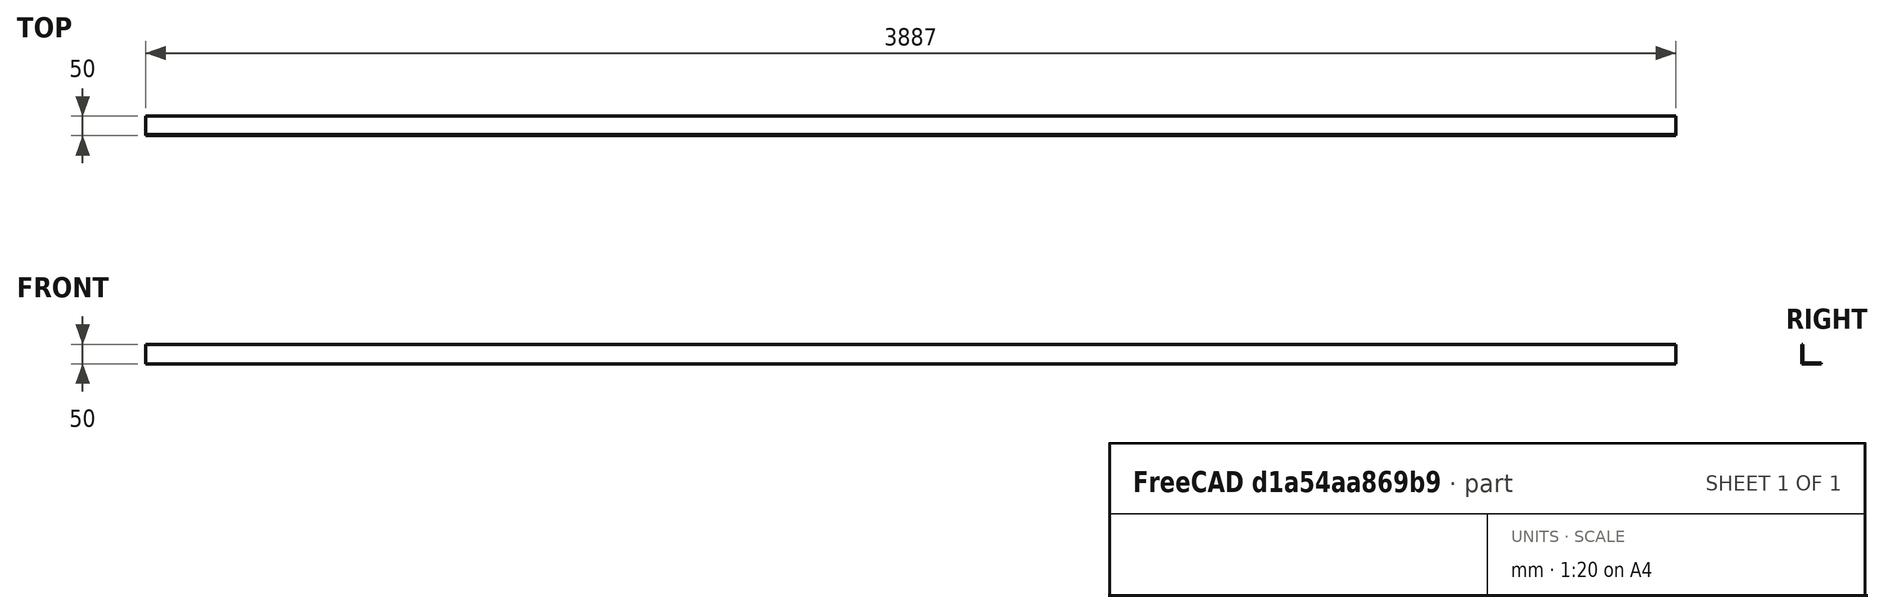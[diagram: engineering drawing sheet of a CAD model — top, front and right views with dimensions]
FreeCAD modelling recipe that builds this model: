
FCSTD DOCUMENT  (FreeCAD 0.18R16131 (Git))
Label: hrazda
License: All rights reserved
LicenseURL: http://en.wikipedia.org/wiki/All_rights_reserved
objects: Sketcher::SketchObject×1, PartDesign::Pad×1, PartDesign::Body×1
note: 4 computed .brp shape members not serialized (recipe doc carries the construction recipe); baked Part::Feature solids carry a one-line shape summary decoded from their .brp

FEATURE [Sketcher::SketchObject] Sketch
  MapMode = 5
  Placement = pos=(0,0,0) rot=(0.57735,0.57735,0.57735;2.0944rad)
  Support = -> [YZ_Plane001]
  sketch-geometry (6):
    g0: LineSegment StartX=-805 StartY=50 StartZ=0 EndX=-805 EndY=0 EndZ=0
    g1: LineSegment StartX=-805 StartY=0 StartZ=0 EndX=-755 EndY=0 EndZ=0
    g2: LineSegment StartX=-755 StartY=0 StartZ=0 EndX=-755 EndY=3 EndZ=0
    g3: LineSegment StartX=-755 StartY=3 StartZ=0 EndX=-802 EndY=3 EndZ=0
    g4: LineSegment StartX=-802 StartY=3 StartZ=0 EndX=-802 EndY=50 EndZ=0
    g5: LineSegment StartX=-802 StartY=50 StartZ=0 EndX=-805 EndY=50 EndZ=0
  constraints (18):
    c: Coincident(g0,g1)
    c: Coincident(g1,g2)
    c: Coincident(g2,g3)
    c: Coincident(g3,g4)
    c: Coincident(g4,g5)
    c: Vertical(g4)
    c: Vertical(g0)
    c: Vertical(g2)
    c: Coincident(g5,g0)
    c: Horizontal(g5)
    c: Horizontal(g1)
    c: Horizontal(g3)
    c: Equal(g5,g2)
    c: DistanceX(g5,g5) = 3
    c: DistanceY(g0,g0) = 50
    c: Equal(g0,g1)
    c: DistanceX(g0,g-1) = 805
    c: DistanceY(g-1,g0) = 0
FEATURE [PartDesign::Pad] Pad
  Length = 3887
  Length2 = 100
  Midplane = true
  Placement = pos=(0,0,0) rot=(0.57735,0.57735,0.57735;2.0944rad)
  Profile = -> Sketch
  Type = 0
FEATURE [PartDesign::Body] Body
  Group = -> [Sketch,Pad]
  Origin = -> Origin001
  Tip = -> Pad
